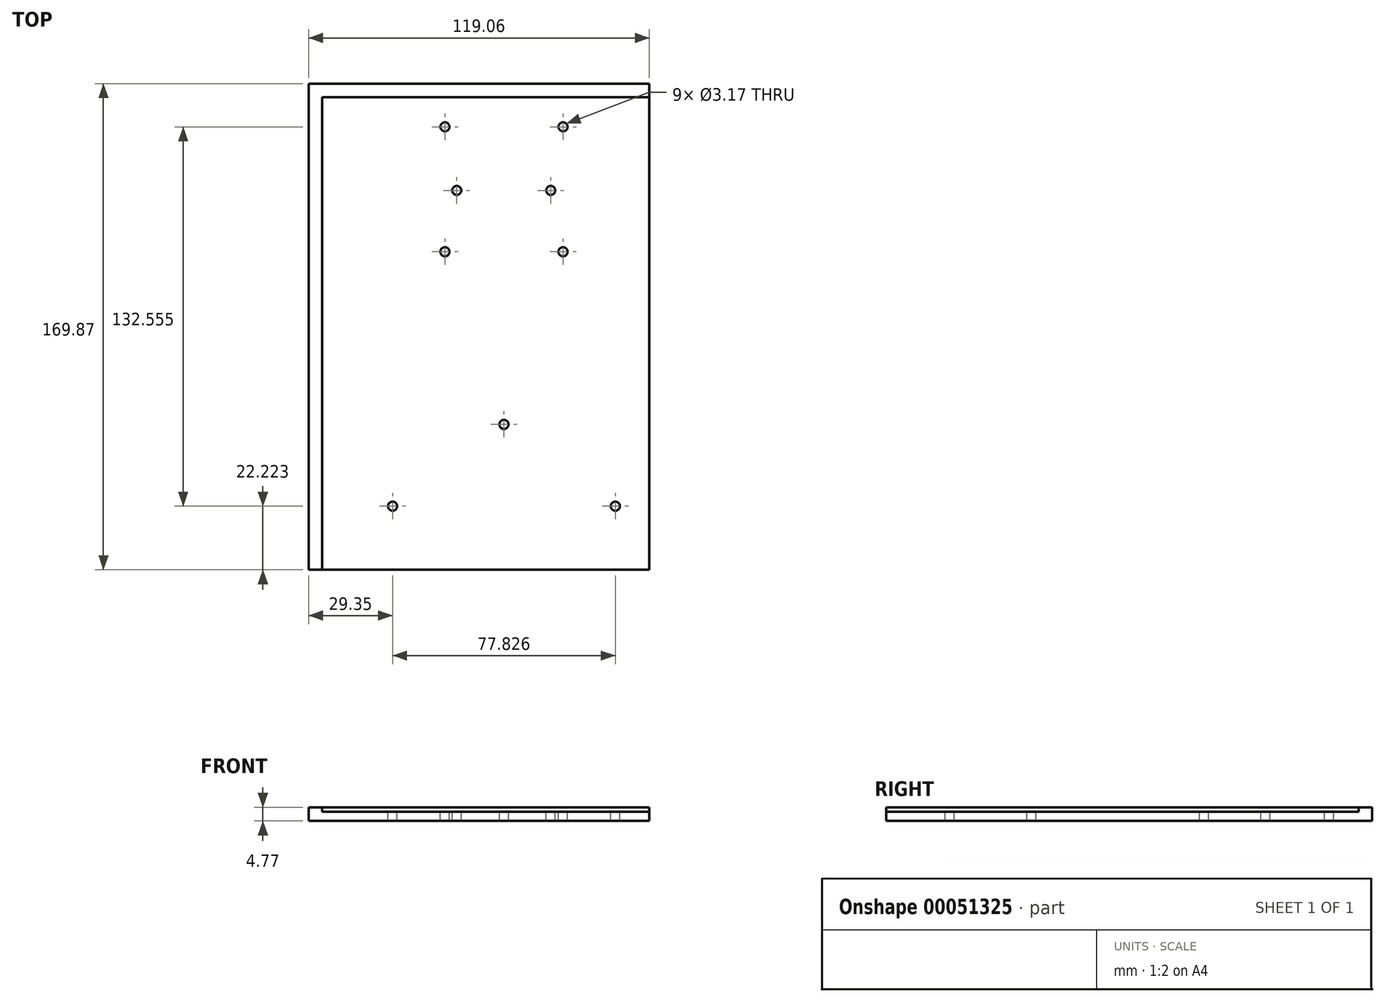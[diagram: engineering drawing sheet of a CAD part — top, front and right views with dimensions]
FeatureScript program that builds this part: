
annotation { "Feature Type Name" : "Feature", "Feature Type Description" : "" }
export const myFeature = defineFeature(function(context is Context, id is Id, definition is map)
    precondition{}
    {
        {
            var Q0;
            Q0=qCreatedBy(makeId("Top.planeOp"),FACE);
            var sketch = newSketch(context, id + "F0", { "sketchPlane" : qUnion([Q0])});
            skLineSegment(sketch, "E0.top", {"start": v(-68.26, 79.04) * mm, "end": v(46.04, 79.04) * mm});
            skLineSegment(sketch, "E0.left", {"start": v(-68.26, -86.06) * mm, "end": v(-68.26, 79.04) * mm});
            skCircle(sketch, "E1", {"center": v(-25.4, 68.72) * mm, "radius": 1.59 * mm});
            skCircle(sketch, "E2", {"center": v(15.88, 68.72) * mm, "radius": 1.59 * mm});
            skCircle(sketch, "E3", {"center": v(-25.4, 25.06) * mm, "radius": 1.59 * mm});
            skCircle(sketch, "E4", {"center": v(15.88, 25.06) * mm, "radius": 1.59 * mm});
            skCircle(sketch, "E5", {"center": v(-21.25, 46.5) * mm, "radius": 1.59 * mm});
            skCircle(sketch, "E6", {"center": v(11.59, 46.5) * mm, "radius": 1.59 * mm});
            skCircle(sketch, "E7", {"center": v(-4.76, -35.26) * mm, "radius": 1.59 * mm});
            skPoint(sketch, "E7.centerSnap0", {"position": v(-4.76, -98.76) * mm});
            skCircle(sketch, "E8", {"center": v(-43.67, -63.84) * mm, "radius": 1.59 * mm});
            skCircle(sketch, "E9", {"center": v(34.16, -63.84) * mm, "radius": 1.59 * mm});
            skLineSegment(sketch, "E10", {"start": v(-73.02, -86.06) * mm, "end": v(-73.02, 83.81) * mm});
            skLineSegment(sketch, "E11", {"start": v(-73.02, 83.81) * mm, "end": v(46.04, 83.81) * mm});
            skLineSegment(sketch, "E12", {"start": v(58.61, 83.81) * mm, "end": v(58.74, 83.81) * mm});
            skLineSegment(sketch, "E13", {"start": v(-73.02, -86.06) * mm, "end": v(46.04, -86.06) * mm});
            skLineSegment(sketch, "E14", {"start": v(46.04, -86.06) * mm, "end": v(46.04, 83.81) * mm});
            skPoint(sketch, "E15.orphan", {"position": v(-68.26, -98.76) * mm});
            skPoint(sketch, "E0.bottom.end.orphan", {"position": v(58.74, -98.76) * mm});
            skPoint(sketch, "E16.start.orphan", {"position": v(58.74, 79.04) * mm});
            skSolve(sketch);
        }
        {
            var Q0;
            {var subQ0=sQuery(id+"F0.wireOp",EDGE,"E0.top");Q0=makeQuery(id+"F0.imprint","IMPRINT",FACE,{"disambiguationData":[TD([[makeQuery(id+"F0.imprint","IMPRINT",EDGE,{"derivedFrom":subQ0}),-1.0]])]});}
            var Q1;
            {var subQ2=sQuery(id+"F0.wireOp",EDGE,"E0.top");Q1=makeQuery(id+"F0.imprint","IMPRINT",FACE,{"disambiguationData":[TD([[makeQuery(id+"F0.imprint","IMPRINT",EDGE,{"derivedFrom":subQ2}),1.0]])]});}
            extrude(context, id + "F1", {"entities" : qUnion([Q0, Q1]), "oppositeDirection" : true, "depth" : 3.17 * mm});
        }
        {
            var Q0;
            {var subQ2=sQuery(id+"F0.wireOp",EDGE,"E0.top");Q0=makeQuery(id+"F0.imprint","IMPRINT",FACE,{"disambiguationData":[TD([[makeQuery(id+"F0.imprint","IMPRINT",EDGE,{"derivedFrom":subQ2}),1.0]])]});}
            extrude(context, id + "F2", {"entities" : qUnion([Q0]), "operationType" : NewBodyOperationType.ADD, "depth" : 1.59 * mm});
        }
    });
